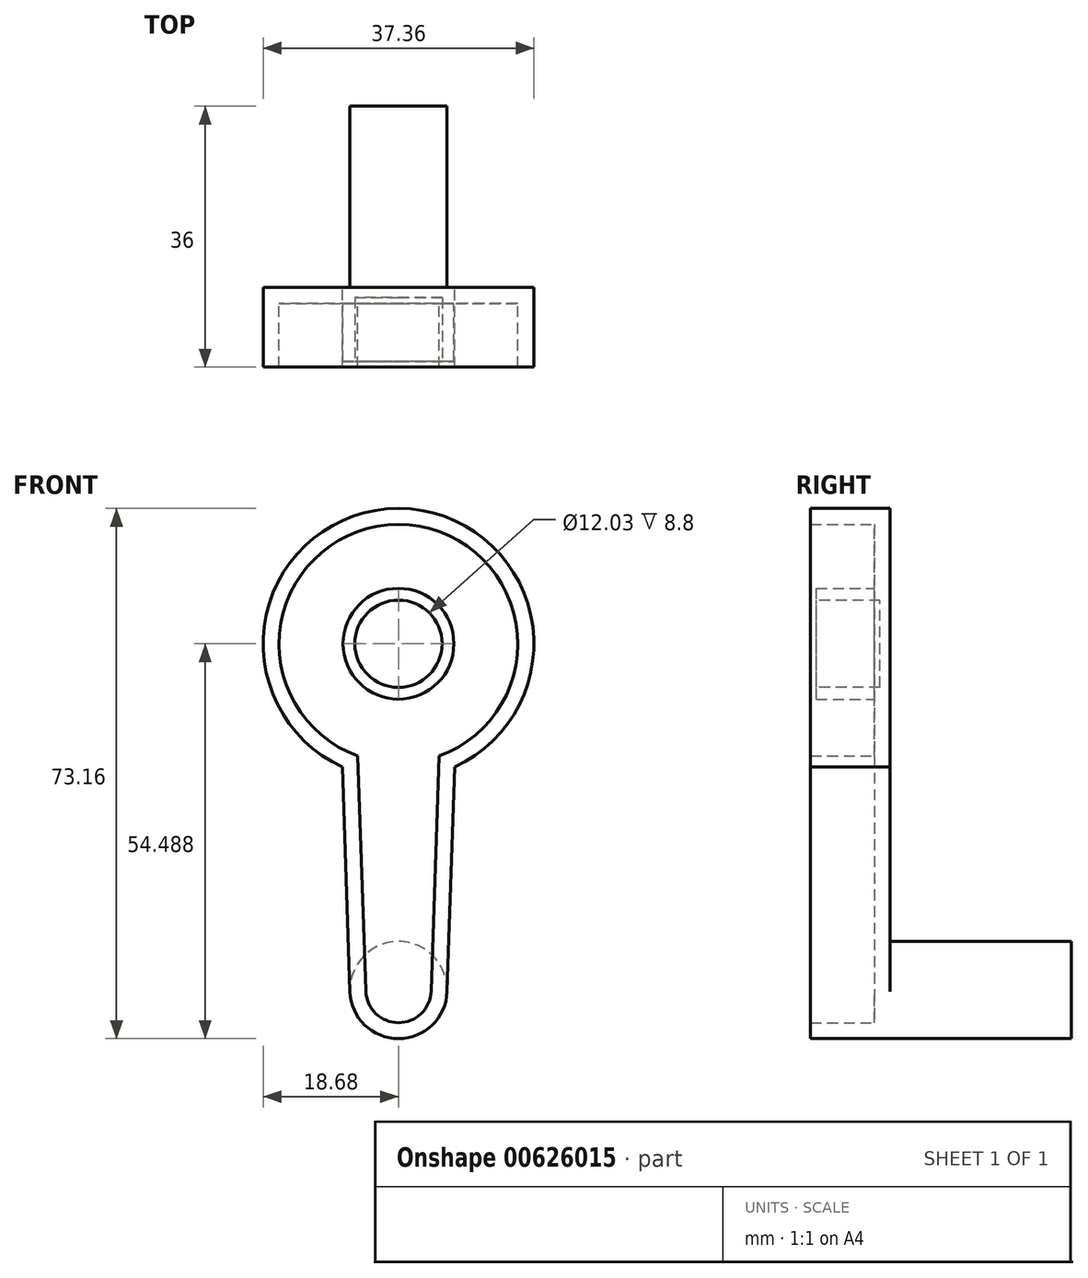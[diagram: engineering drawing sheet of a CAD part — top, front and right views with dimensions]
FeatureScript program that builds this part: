
annotation { "Feature Type Name" : "Feature", "Feature Type Description" : "" }
export const myFeature = defineFeature(function(context is Context, id is Id, definition is map)
    precondition{}
    {
        {
            var Q0;
            Q0=qCreatedBy(makeId("Front.planeOp"),FACE);
            var sketch = newSketch(context, id + "F0", { "sketchPlane" : qUnion([Q0])});
            skArc(sketch, "E0", {"start": v(7.75, 17.34) * mm, "mid": v(0, 53) * mm, "end": v(-7.76, 17.34) * mm});
            skArc(sketch, "E1", {"start": v(8.3, 33.54) * mm, "mid": v(0.25, 42.66) * mm, "end": v(-8.33, 34.04) * mm});
            skCircle(sketch, "E2", {"center": v(0, -13.46) * mm, "radius": 6.7 * mm});
            skLineSegment(sketch, "E3", {"start": v(-7.76, 17.34) * mm, "end": v(-6.7, -13.69) * mm});
            skLineSegment(sketch, "E4", {"start": v(8.33, 34.56) * mm, "end": v(8.3, 33.54) * mm});
            skCircle(sketch, "E5", {"center": v(0, 34.33) * mm, "radius": 5.02 * mm});
            skLineSegment(sketch, "E6.trimOffspring", {"start": v(7.75, 17.34) * mm, "end": v(6.7, -13.68) * mm});
            skSolve(sketch);
        }
        {
            var Q0;
            Q0 = qSketchRegion(id + "F0", true);
            var Q1;
            {var subQ0=sQuery(id+"F0.wireOp",EDGE,"E1");var subQ1=makeQuery(id+"F0.imprint","INTERSECT",VERTEX,{"derivedFrom":[subQ0,sQuery(id+"F0.wireOp",EDGE,"E3")]});Q1=makeQuery(id+"F0.imprint","IMPRINT",FACE,{"disambiguationData":[TD([[makeQuery(id+"F0.imprint","IMPRINT",EDGE,{"disambiguationData":[TD([[subQ1,1.0]])],"derivedFrom":subQ0}),1.0]])]});}
            var Q2;
            Q2=makeQuery(id+"F0.imprint","IMPRINT",FACE,{"disambiguationData":[TD([[makeQuery(id+"F0.imprint","IMPRINT",EDGE,{"derivedFrom":sQuery(id+"F0.wireOp",EDGE,"E5")}),1.0]])]});
            extrude(context, id + "F1", {"entities" : qUnion([Q0, Q1, Q2]), "depth" : 11 * mm, "offsetDistance" : 25 * mm});
        }
        {
            var Q0;
            Q0=makeQuery(id+"F1.opExtrude","CAP_FACE",FACE,{"disambiguationData":[OSD([sQuery(id+"F0.wireOp",EDGE,"E0"),sQuery(id+"F0.wireOp",EDGE,"E1"),sQuery(id+"F0.wireOp",EDGE,"E2"),sQuery(id+"F0.wireOp",EDGE,"E3"),sQuery(id+"F0.wireOp",EDGE,"E4")])],"isStart":false});
            shell(context, id + "F2", {"entities" : qUnion([Q0]), "thickness" : 2.2 * mm});
        }
        {
            var Q0;
            Q0=makeQuery(id+"F2.opShell","OFFSET_FACE",FACE,{"disambiguationData":[OSD([sQuery(id+"F0.wireOp",EDGE,"E0"),sQuery(id+"F0.wireOp",EDGE,"E2"),sQuery(id+"F0.wireOp",EDGE,"E3"),sQuery(id+"F0.wireOp",EDGE,"E6.trimOffspring")])]});
            var sketch = newSketch(context, id + "F3", { "sketchPlane" : qUnion([Q0])});
            skCircle(sketch, "E7", {"center": v(0, 34.33) * mm, "radius": 7.64 * mm});
            skSolve(sketch);
        }
        {
            var Q0;
            Q0=makeQuery(id+"F3.imprint","IMPRINT",FACE,{"disambiguationData":[TD([[makeQuery(id+"F3.imprint","IMPRINT",EDGE,{"derivedFrom":sQuery(id+"F3.wireOp",EDGE,"E7")}),1.0]])]});
            extrude(context, id + "F4", {"entities" : qUnion([Q0]), "operationType" : NewBodyOperationType.ADD, "depth" : 8 * mm, "offsetDistance" : 25 * mm});
        }
        {
            var Q0;
            Q0=makeQuery(id+"F4.opExtrude","CAP_FACE",FACE,{"disambiguationData":[OSD([sQuery(id+"F3.wireOp",EDGE,"E7")])],"isStart":false});
            var sketch = newSketch(context, id + "F5", { "sketchPlane" : qUnion([Q0])});
            skCircle(sketch, "E8", {"center": v(0, 34.33) * mm, "radius": 6.02 * mm});
            skSolve(sketch);
        }
        {
            var Q0;
            Q0=makeQuery(id+"F5.imprint","IMPRINT",FACE,{"disambiguationData":[TD([[makeQuery(id+"F5.imprint","IMPRINT",EDGE,{"derivedFrom":sQuery(id+"F5.wireOp",EDGE,"E8")}),1.0]])]});
            extrude(context, id + "F6", {"entities" : qUnion([Q0]), "operationType" : NewBodyOperationType.REMOVE, "oppositeDirection" : true, "depth" : 8.8 * mm, "offsetDistance" : 25 * mm});
        }
        {
            var Q0;
            {var subQ0=sQuery(id+"F0.wireOp",EDGE,"E2");var subQ1=makeQuery(id+"F0.imprint","INTERSECT",VERTEX,{"derivedFrom":[subQ0,sQuery(id+"F0.wireOp",EDGE,"E3")]});Q0=makeQuery(id+"F0.imprint","IMPRINT",FACE,{"disambiguationData":[TD([[makeQuery(id+"F0.imprint","IMPRINT",EDGE,{"disambiguationData":[TD([[subQ1,-1.0]])],"derivedFrom":subQ0}),1.0]])]});}
            extrude(context, id + "F7", {"entities" : qUnion([Q0]), "operationType" : NewBodyOperationType.ADD, "oppositeDirection" : true, "depth" : 25 * mm, "offsetDistance" : 25 * mm});
        }
    });
